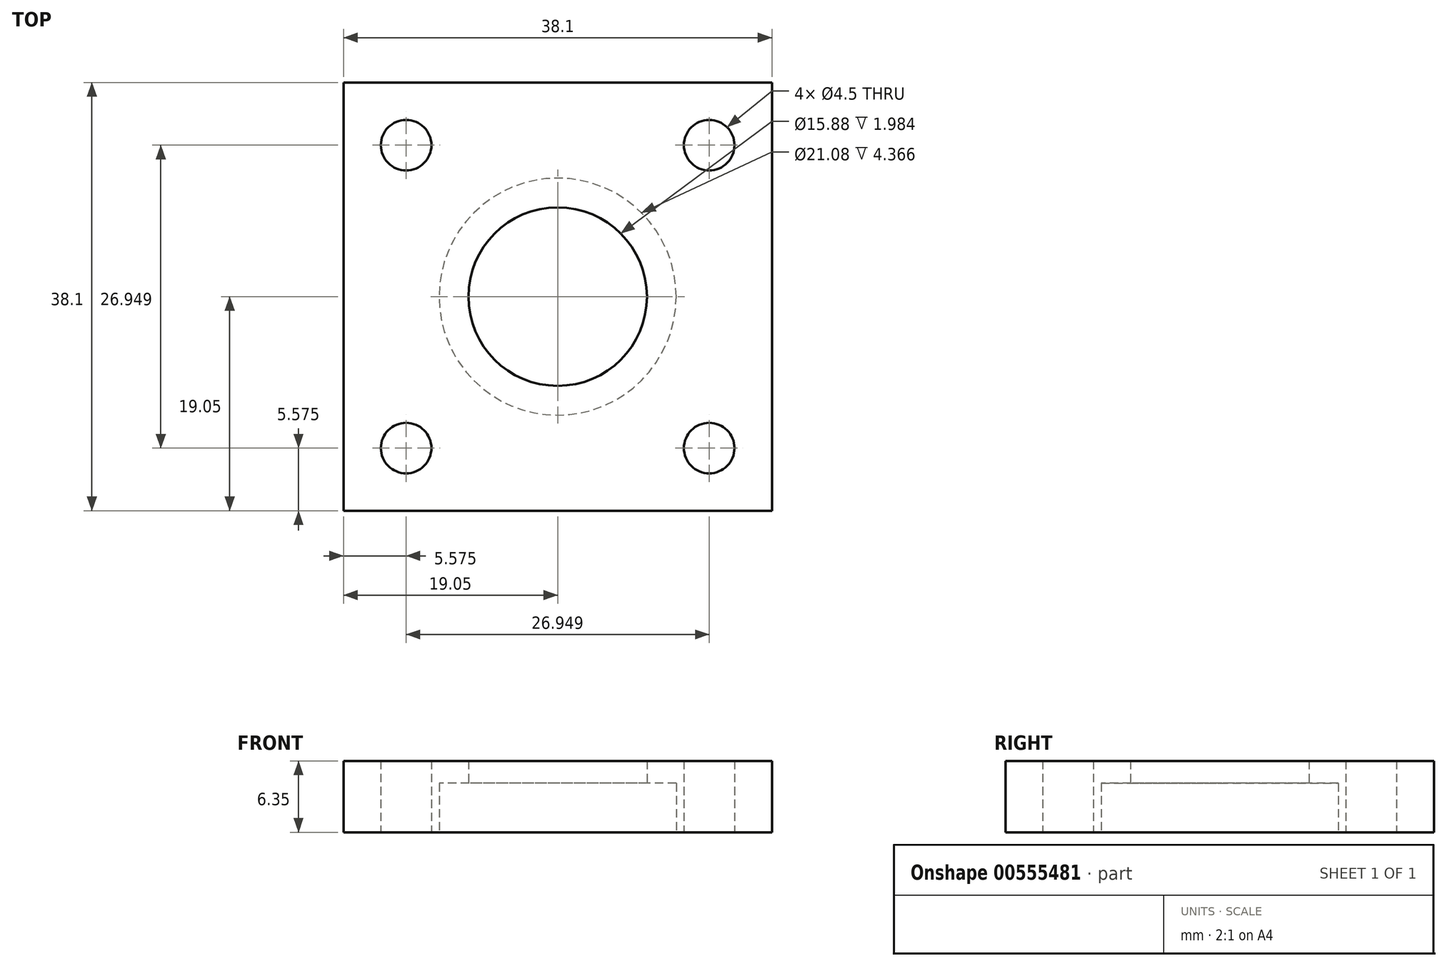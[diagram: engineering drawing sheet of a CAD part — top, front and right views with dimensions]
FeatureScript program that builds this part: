
annotation { "Feature Type Name" : "Feature", "Feature Type Description" : "" }
export const myFeature = defineFeature(function(context is Context, id is Id, definition is map)
    precondition{}
    {
        {
            var Q0;
            Q0=qCreatedBy(makeId("Top.planeOp"),FACE);
            var sketch = newSketch(context, id + "F0", { "sketchPlane" : qUnion([Q0])});
            skLineSegment(sketch, "E0.bottom", {"start": v(-19.05, 19.05) * mm, "end": v(19.05, 19.05) * mm});
            skLineSegment(sketch, "E0.top", {"start": v(-19.05, -19.05) * mm, "end": v(19.05, -19.05) * mm});
            skLineSegment(sketch, "E0.left", {"start": v(-19.05, 19.05) * mm, "end": v(-19.05, -19.05) * mm});
            skLineSegment(sketch, "E0.right", {"start": v(19.05, 19.05) * mm, "end": v(19.05, -19.05) * mm});
            skPoint(sketch, "E0.middle", {"position": v(0, 0) * mm});
            skLineSegment(sketch, "E1", {"start": v(-19.05, 13.47) * mm, "end": v(19.05, 13.47) * mm, "construction": true});
            skLineSegment(sketch, "E2", {"start": v(-13.47, 19.05) * mm, "end": v(-13.47, -19.05) * mm, "construction": true});
            skLineSegment(sketch, "E3", {"start": v(13.47, 19.05) * mm, "end": v(13.47, -19.05) * mm, "construction": true});
            skLineSegment(sketch, "E4", {"start": v(-19.05, -13.47) * mm, "end": v(19.05, -13.47) * mm, "construction": true});
            skLineSegment(sketch, "E5", {"start": v(-19.05, 0) * mm, "end": v(19.05, 0) * mm, "construction": true});
            skCircle(sketch, "E6", {"center": v(0, 0) * mm, "radius": 10.54 * mm});
            skPoint(sketch, "E7", {"position": v(-13.47, -13.47) * mm});
            skPoint(sketch, "E8", {"position": v(-13.47, 13.47) * mm});
            skPoint(sketch, "E9", {"position": v(13.47, 13.47) * mm});
            skPoint(sketch, "E10", {"position": v(13.47, -13.47) * mm});
            skCircle(sketch, "E11", {"center": v(0, 0) * mm, "radius": 7.94 * mm});
            skSolve(sketch);
        }
        {
            var Q0;
            {var subQ0=sQuery(id+"F0.wireOp",EDGE,"E0.right");Q0=makeQuery(id+"F0.imprint","IMPRINT",FACE,{"disambiguationData":[TD([[makeQuery(id+"F0.imprint","IMPRINT",EDGE,{"derivedFrom":subQ0}),-1.0]])]});}
            extrude(context, id + "F1", {"entities" : qUnion([Q0]), "depth" : 6.35 * mm, "offsetDistance" : 25.4 * mm});
        }
        {
            var Q0;
            {var subQ1=sQuery(id+"F0.wireOp",EDGE,"E0.left");Q0=makeQuery(id+"F0.imprint","IMPRINT",FACE,{"disambiguationData":[TD([[makeQuery(id+"F0.imprint","IMPRINT",EDGE,{"derivedFrom":subQ1}),1.0]])]});}
            var Q1;
            Q1=makeQuery(id+"F0.imprint","IMPRINT",FACE,{"disambiguationData":[TD([[makeQuery(id+"F0.imprint","IMPRINT",EDGE,{"derivedFrom":sQuery(id+"F0.wireOp",EDGE,"E6")}),1.0]])]});
            extrude(context, id + "F2", {"entities" : qUnion([Q0, Q1]), "operationType" : NewBodyOperationType.ADD, "depth" : 6.35 * mm, "offsetDistance" : 25.4 * mm});
        }
        {
            var Q0;
            Q0=sQuery(id+"F0.wireOp",VERTEX,"E7");
            var Q1;
            Q1=makeQuery(id+"F1.opExtrude","SWEPT_BODY",BODY,{"disambiguationData":[OSD([sQuery(id+"F0.wireOp",EDGE,"E0.bottom"),sQuery(id+"F0.wireOp",EDGE,"E0.top"),sQuery(id+"F0.wireOp",EDGE,"E0.right"),sQuery(id+"F0.wireOp",EDGE,"H2lXDhBS-bBmv-jnvt-dtpl-yNRelDX2eWJu")])]});
            hole(context, id + "F3", {"style" : HoleStyle.SIMPLE, "endStyle" : HoleEndStyle.THROUGH, "oppositeDirection" : true, "standardTappedOrClearance" : lookupTablePath({ "standard" : "ANSI", "fit" : "Normal (ASME)", "size" : "#8", "type" : "Clearance" }), "standardBlindInLast" : lookupTablePath({ "fit" : "Free", "standard" : "ANSI", "size" : "#8", "type" : "Clearance" }), "holeDiameter" : 4.5 * mm, "isTappedThrough" : true, "tappedDepth" : 12.7 * mm, "tapClearance" : 3, "locations" : qUnion([Q0]), "scope" : qUnion([Q1])});
        }
        {
            var Q0;
            Q0=sQuery(id+"F0.wireOp",VERTEX,"E8");
            var Q1;
            Q1=makeQuery(id+"F1.opExtrude","SWEPT_BODY",BODY,{"disambiguationData":[OSD([sQuery(id+"F0.wireOp",EDGE,"E0.bottom"),sQuery(id+"F0.wireOp",EDGE,"E0.top"),sQuery(id+"F0.wireOp",EDGE,"E0.right"),sQuery(id+"F0.wireOp",EDGE,"H2lXDhBS-bBmv-jnvt-dtpl-yNRelDX2eWJu")])]});
            hole(context, id + "F4", {"style" : HoleStyle.SIMPLE, "endStyle" : HoleEndStyle.THROUGH, "oppositeDirection" : true, "standardTappedOrClearance" : lookupTablePath({ "standard" : "ANSI", "fit" : "Normal (ASME)", "size" : "#8", "type" : "Clearance" }), "standardBlindInLast" : lookupTablePath({ "fit" : "Free", "standard" : "ANSI", "size" : "#8", "type" : "Clearance" }), "holeDiameter" : 4.5 * mm, "isTappedThrough" : true, "tappedDepth" : 12.7 * mm, "tapClearance" : 3, "locations" : qUnion([Q0]), "scope" : qUnion([Q1])});
        }
        {
            var Q0;
            Q0=sQuery(id+"F0.wireOp",VERTEX,"E9");
            var Q1;
            Q1=makeQuery(id+"F1.opExtrude","SWEPT_BODY",BODY,{"disambiguationData":[OSD([sQuery(id+"F0.wireOp",EDGE,"E0.bottom"),sQuery(id+"F0.wireOp",EDGE,"E0.top"),sQuery(id+"F0.wireOp",EDGE,"E0.right"),sQuery(id+"F0.wireOp",EDGE,"H2lXDhBS-bBmv-jnvt-dtpl-yNRelDX2eWJu")])]});
            hole(context, id + "F5", {"style" : HoleStyle.SIMPLE, "endStyle" : HoleEndStyle.THROUGH, "oppositeDirection" : true, "standardTappedOrClearance" : lookupTablePath({ "standard" : "ANSI", "fit" : "Normal (ASME)", "size" : "#8", "type" : "Clearance" }), "standardBlindInLast" : lookupTablePath({ "fit" : "Free", "standard" : "ANSI", "size" : "#8", "type" : "Clearance" }), "holeDiameter" : 4.5 * mm, "isTappedThrough" : true, "tappedDepth" : 12.7 * mm, "tapClearance" : 3, "locations" : qUnion([Q0]), "scope" : qUnion([Q1])});
        }
        {
            var Q0;
            Q0=sQuery(id+"F0.wireOp",VERTEX,"E10");
            var Q1;
            Q1=makeQuery(id+"F1.opExtrude","SWEPT_BODY",BODY,{"disambiguationData":[OSD([sQuery(id+"F0.wireOp",EDGE,"E0.bottom"),sQuery(id+"F0.wireOp",EDGE,"E0.top"),sQuery(id+"F0.wireOp",EDGE,"E0.right"),sQuery(id+"F0.wireOp",EDGE,"H2lXDhBS-bBmv-jnvt-dtpl-yNRelDX2eWJu")])]});
            hole(context, id + "F6", {"style" : HoleStyle.SIMPLE, "endStyle" : HoleEndStyle.THROUGH, "oppositeDirection" : true, "standardTappedOrClearance" : lookupTablePath({ "standard" : "ANSI", "fit" : "Normal (ASME)", "size" : "#8", "type" : "Clearance" }), "standardBlindInLast" : lookupTablePath({ "fit" : "Free", "standard" : "ANSI", "size" : "#8", "type" : "Clearance" }), "holeDiameter" : 4.5 * mm, "isTappedThrough" : true, "tappedDepth" : 12.7 * mm, "tapClearance" : 3, "locations" : qUnion([Q0]), "scope" : qUnion([Q1])});
        }
        {
            var Q0;
            Q0=makeQuery(id+"F0.imprint","IMPRINT",FACE,{"disambiguationData":[TD([[makeQuery(id+"F0.imprint","IMPRINT",EDGE,{"derivedFrom":sQuery(id+"F0.wireOp",EDGE,"E6")}),1.0]])]});
            extrude(context, id + "F7", {"entities" : qUnion([Q0]), "operationType" : NewBodyOperationType.REMOVE, "depth" : 4.37 * mm, "offsetDistance" : 25.4 * mm});
        }
    });
